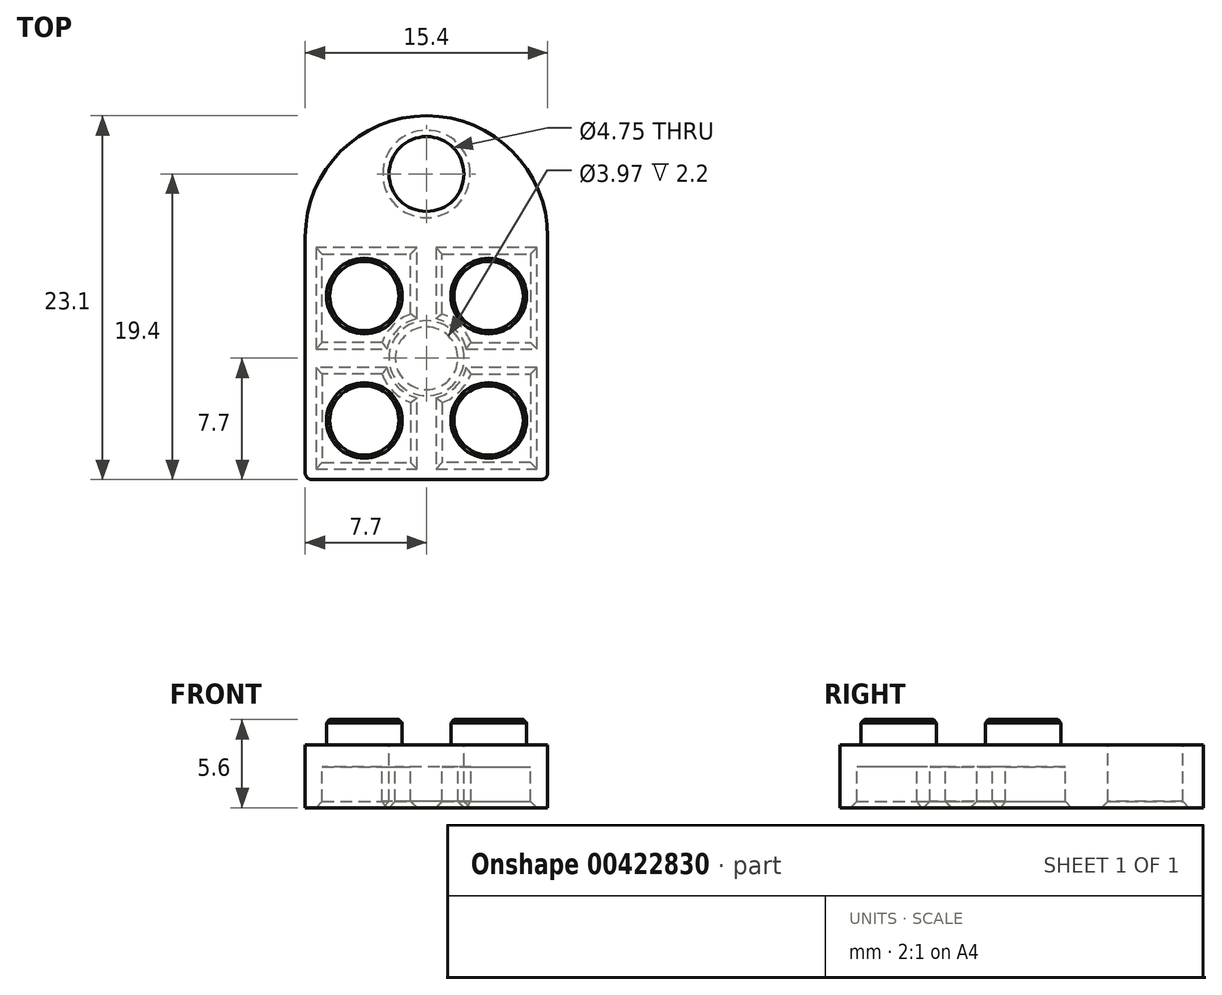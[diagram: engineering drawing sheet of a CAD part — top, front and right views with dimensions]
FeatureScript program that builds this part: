
annotation { "Feature Type Name" : "Feature", "Feature Type Description" : "" }
export const myFeature = defineFeature(function(context is Context, id is Id, definition is map)
    precondition{}
    {
        {
            var Q0;
            Q0=qCreatedBy(makeId("Top.planeOp"),FACE);
            var sketch = newSketch(context, id + "F0", { "sketchPlane" : qUnion([Q0])});
            skLineSegment(sketch, "E0.bottom", {"start": v(-7.7, 7.7) * mm, "end": v(7.7, 7.7) * mm});
            skLineSegment(sketch, "E0.top", {"start": v(-7.7, -7.7) * mm, "end": v(7.7, -7.7) * mm});
            skLineSegment(sketch, "E0.left", {"start": v(-7.7, 7.7) * mm, "end": v(-7.7, -7.7) * mm});
            skLineSegment(sketch, "E0.right", {"start": v(7.7, 7.7) * mm, "end": v(7.7, -7.7) * mm});
            skLineSegment(sketch, "E1", {"start": v(-7.7, 7.7) * mm, "end": v(7.7, -7.7) * mm, "construction": true});
            skArc(sketch, "E2", {"start": v(7.7, 7.7) * mm, "mid": v(0, 15.4) * mm, "end": v(-7.7, 7.7) * mm});
            skLineSegment(sketch, "E3", {"start": v(7.7, 7.7) * mm, "end": v(-7.7, -7.7) * mm, "construction": true});
            skLineSegment(sketch, "E4.bottom", {"start": v(-3.95, 3.95) * mm, "end": v(3.95, 3.95) * mm, "construction": true});
            skLineSegment(sketch, "E4.top", {"start": v(-3.95, -3.95) * mm, "end": v(3.95, -3.95) * mm, "construction": true});
            skLineSegment(sketch, "E4.left", {"start": v(-3.95, 3.95) * mm, "end": v(-3.95, -3.95) * mm, "construction": true});
            skLineSegment(sketch, "E4.right", {"start": v(3.95, 3.95) * mm, "end": v(3.95, -3.95) * mm, "construction": true});
            skCircle(sketch, "E5", {"center": v(3.95, 3.95) * mm, "radius": 2.4 * mm});
            skCircle(sketch, "E6", {"center": v(-3.95, 3.95) * mm, "radius": 2.4 * mm});
            skCircle(sketch, "E7", {"center": v(-3.95, -3.95) * mm, "radius": 2.4 * mm});
            skCircle(sketch, "E8", {"center": v(3.95, -3.95) * mm, "radius": 2.4 * mm});
            skLineSegment(sketch, "E9.bottom", {"start": v(-6.35, 6.35) * mm, "end": v(6.35, 6.35) * mm});
            skLineSegment(sketch, "E9.top", {"start": v(-6.35, -6.35) * mm, "end": v(6.35, -6.35) * mm});
            skLineSegment(sketch, "E9.left", {"start": v(-6.35, 6.35) * mm, "end": v(-6.35, -6.35) * mm});
            skLineSegment(sketch, "E9.right", {"start": v(6.35, 6.35) * mm, "end": v(6.35, -6.35) * mm});
            skCircle(sketch, "E10", {"center": v(0, 11.7) * mm, "radius": 2.38 * mm});
            skCircle(sketch, "E11", {"center": v(0, 0) * mm, "radius": 2.99 * mm});
            skCircle(sketch, "E12", {"center": v(0, 0) * mm, "radius": 1.99 * mm});
            skLineSegment(sketch, "E13.bottom", {"start": v(-6.62, 6.62) * mm, "end": v(6.62, 6.62) * mm});
            skLineSegment(sketch, "E13.top", {"start": v(-6.62, -6.62) * mm, "end": v(6.62, -6.62) * mm});
            skLineSegment(sketch, "E13.left", {"start": v(-6.62, 6.62) * mm, "end": v(-6.62, -6.62) * mm});
            skLineSegment(sketch, "E13.right", {"start": v(6.62, 6.62) * mm, "end": v(6.62, -6.62) * mm});
            skSolve(sketch);
        }
        {
            var Q0;
            Q0=makeQuery(id+"F0.imprint","IMPRINT",FACE,{"disambiguationData":[TD([[makeQuery(id+"F0.imprint","IMPRINT",EDGE,{"derivedFrom":sQuery(id+"F0.wireOp",EDGE,"E0.bottom")}),1.0]])]});
            var Q1;
            Q1=makeQuery(id+"F0.imprint","IMPRINT",FACE,{"disambiguationData":[TD([[makeQuery(id+"F0.imprint","IMPRINT",EDGE,{"derivedFrom":sQuery(id+"F0.wireOp",EDGE,"E5")}),1.0]])]});
            var Q2;
            Q2=makeQuery(id+"F0.imprint","IMPRINT",FACE,{"disambiguationData":[TD([[makeQuery(id+"F0.imprint","IMPRINT",EDGE,{"derivedFrom":sQuery(id+"F0.wireOp",EDGE,"E6")}),1.0]])]});
            var Q3;
            Q3=makeQuery(id+"F0.imprint","IMPRINT",FACE,{"disambiguationData":[TD([[makeQuery(id+"F0.imprint","IMPRINT",EDGE,{"derivedFrom":sQuery(id+"F0.wireOp",EDGE,"E7")}),1.0]])]});
            var Q4;
            Q4=makeQuery(id+"F0.imprint","IMPRINT",FACE,{"disambiguationData":[TD([[makeQuery(id+"F0.imprint","IMPRINT",EDGE,{"derivedFrom":sQuery(id+"F0.wireOp",EDGE,"E8")}),1.0]])]});
            var Q5;
            Q5=makeQuery(id+"F0.imprint","IMPRINT",FACE,{"disambiguationData":[TD([[makeQuery(id+"F0.imprint","IMPRINT",EDGE,{"derivedFrom":sQuery(id+"F0.wireOp",EDGE,"E0.bottom")}),-1.0]])]});
            var Q6;
            {var subQ5=sQuery(id+"F0.wireOp",EDGE,"E9.bottom");var subQ13=sQuery(id+"F0.wireOp",EDGE,"E5");var subQ14=makeQuery(id+"F0.imprint","INTERSECT",VERTEX,{"derivedFrom":[subQ13,subQ5]});Q6=makeQuery(id+"F0.imprint","IMPRINT",FACE,{"disambiguationData":[TD([[makeQuery(id+"F0.imprint","IMPRINT",EDGE,{"disambiguationData":[TD([[subQ14,-1.0]])],"derivedFrom":subQ13}),-1.0]])]});}
            var Q7;
            {var subQ0=sQuery(id+"F0.wireOp",EDGE,"E9.top");var subQ1=sQuery(id+"F0.wireOp",EDGE,"E7");var subQ2=makeQuery(id+"F0.imprint","INTERSECT",VERTEX,{"derivedFrom":[subQ1,subQ0]});Q7=makeQuery(id+"F0.imprint","IMPRINT",FACE,{"disambiguationData":[TD([[makeQuery(id+"F0.imprint","IMPRINT",EDGE,{"disambiguationData":[TD([[subQ2,1.0]])],"derivedFrom":subQ1}),-1.0]])]});}
            var Q8;
            {var subQ0=sQuery(id+"F0.wireOp",EDGE,"E9.bottom");var subQ1=sQuery(id+"F0.wireOp",EDGE,"E6");var subQ2=makeQuery(id+"F0.imprint","INTERSECT",VERTEX,{"derivedFrom":[subQ1,subQ0]});Q8=makeQuery(id+"F0.imprint","IMPRINT",FACE,{"disambiguationData":[TD([[makeQuery(id+"F0.imprint","IMPRINT",EDGE,{"disambiguationData":[TD([[subQ2,-1.0]])],"derivedFrom":subQ1}),-1.0]])]});}
            var Q9;
            {var subQ0=sQuery(id+"F0.wireOp",EDGE,"E9.bottom");var subQ1=sQuery(id+"F0.wireOp",EDGE,"E5");var subQ2=makeQuery(id+"F0.imprint","INTERSECT",VERTEX,{"derivedFrom":[subQ1,subQ0]});Q9=makeQuery(id+"F0.imprint","IMPRINT",FACE,{"disambiguationData":[TD([[makeQuery(id+"F0.imprint","IMPRINT",EDGE,{"disambiguationData":[TD([[subQ2,1.0]])],"derivedFrom":subQ1}),-1.0]])]});}
            var Q10;
            {var subQ0=sQuery(id+"F0.wireOp",EDGE,"E9.top");var subQ1=sQuery(id+"F0.wireOp",EDGE,"E8");var subQ2=makeQuery(id+"F0.imprint","INTERSECT",VERTEX,{"derivedFrom":[subQ1,subQ0]});Q10=makeQuery(id+"F0.imprint","IMPRINT",FACE,{"disambiguationData":[TD([[makeQuery(id+"F0.imprint","IMPRINT",EDGE,{"disambiguationData":[TD([[subQ2,-1.0]])],"derivedFrom":subQ1}),-1.0]])]});}
            var Q11;
            {var subQ0=sQuery(id+"F0.wireOp",EDGE,"E9.left");var subQ1=sQuery(id+"F0.wireOp",EDGE,"E6");var subQ2=makeQuery(id+"F0.imprint","INTERSECT",VERTEX,{"derivedFrom":[subQ1,subQ0]});Q11=makeQuery(id+"F0.imprint","IMPRINT",FACE,{"disambiguationData":[TD([[makeQuery(id+"F0.imprint","IMPRINT",EDGE,{"disambiguationData":[TD([[subQ2,-1.0]])],"derivedFrom":subQ1}),-1.0]])]});}
            var Q12;
            {var subQ0=sQuery(id+"F0.wireOp",EDGE,"E9.right");var subQ1=sQuery(id+"F0.wireOp",EDGE,"E5");var subQ2=makeQuery(id+"F0.imprint","INTERSECT",VERTEX,{"derivedFrom":[subQ1,subQ0]});Q12=makeQuery(id+"F0.imprint","IMPRINT",FACE,{"disambiguationData":[TD([[makeQuery(id+"F0.imprint","IMPRINT",EDGE,{"disambiguationData":[TD([[subQ2,1.0]])],"derivedFrom":subQ1}),-1.0]])]});}
            var Q13;
            {var subQ0=sQuery(id+"F0.wireOp",EDGE,"E11");var subQ1=sQuery(id+"F0.wireOp",EDGE,"E7");var subQ2=makeQuery(id+"F0.imprint","INTERSECT",VERTEX,{"derivedFrom":[subQ1,subQ0]});Q13=makeQuery(id+"F0.imprint","IMPRINT",FACE,{"disambiguationData":[TD([[makeQuery(id+"F0.imprint","IMPRINT",EDGE,{"disambiguationData":[TD([[subQ2,1.0]])],"derivedFrom":subQ1}),-1.0]])]});}
            var Q14;
            Q14=makeQuery(id+"F0.imprint","IMPRINT",FACE,{"disambiguationData":[TD([[makeQuery(id+"F0.imprint","IMPRINT",EDGE,{"derivedFrom":sQuery(id+"F0.wireOp",EDGE,"E12")}),-1.0]])]});
            var Q15;
            Q15=makeQuery(id+"F0.imprint","IMPRINT",FACE,{"disambiguationData":[TD([[makeQuery(id+"F0.imprint","IMPRINT",EDGE,{"derivedFrom":sQuery(id+"F0.wireOp",EDGE,"E12")}),1.0]])]});
            var Q16;
            Q16=makeQuery(id+"F0.imprint","IMPRINT",FACE,{"disambiguationData":[TD([[makeQuery(id+"F0.imprint","IMPRINT",EDGE,{"derivedFrom":sQuery(id+"F0.wireOp",EDGE,"E13.bottom")}),-1.0]])]});
            extrude(context, id + "F1", {"entities" : qUnion([Q0, Q1, Q2, Q3, Q4, Q5, Q6, Q7, Q8, Q9, Q10, Q11, Q12, Q13, Q14, Q15, Q16]), "oppositeDirection" : true, "depth" : 1.4 * mm});
        }
        {
            var Q0;
            Q0=makeQuery(id+"F0.imprint","IMPRINT",FACE,{"disambiguationData":[TD([[makeQuery(id+"F0.imprint","IMPRINT",EDGE,{"derivedFrom":sQuery(id+"F0.wireOp",EDGE,"E6")}),1.0]])]});
            var Q1;
            Q1=makeQuery(id+"F0.imprint","IMPRINT",FACE,{"disambiguationData":[TD([[makeQuery(id+"F0.imprint","IMPRINT",EDGE,{"derivedFrom":sQuery(id+"F0.wireOp",EDGE,"E5")}),1.0]])]});
            var Q2;
            Q2=makeQuery(id+"F0.imprint","IMPRINT",FACE,{"disambiguationData":[TD([[makeQuery(id+"F0.imprint","IMPRINT",EDGE,{"derivedFrom":sQuery(id+"F0.wireOp",EDGE,"E8")}),1.0]])]});
            var Q3;
            Q3=makeQuery(id+"F0.imprint","IMPRINT",FACE,{"disambiguationData":[TD([[makeQuery(id+"F0.imprint","IMPRINT",EDGE,{"derivedFrom":sQuery(id+"F0.wireOp",EDGE,"E7")}),1.0]])]});
            extrude(context, id + "F2", {"entities" : qUnion([Q0, Q1, Q2, Q3]), "operationType" : NewBodyOperationType.ADD, "depth" : 1.6 * mm});
        }
        {
            var Q0;
            Q0=makeQuery(id+"F0.imprint","IMPRINT",FACE,{"disambiguationData":[TD([[makeQuery(id+"F0.imprint","IMPRINT",EDGE,{"derivedFrom":sQuery(id+"F0.wireOp",EDGE,"E12")}),-1.0]])]});
            var Q1;
            Q1=makeQuery(id+"F0.imprint","IMPRINT",FACE,{"disambiguationData":[TD([[makeQuery(id+"F0.imprint","IMPRINT",EDGE,{"derivedFrom":sQuery(id+"F0.wireOp",EDGE,"E0.bottom")}),-1.0]])]});
            var Q2;
            Q2=makeQuery(id+"F0.imprint","IMPRINT",FACE,{"disambiguationData":[TD([[makeQuery(id+"F0.imprint","IMPRINT",EDGE,{"derivedFrom":sQuery(id+"F0.wireOp",EDGE,"E0.bottom")}),1.0]])]});
            extrude(context, id + "F3", {"entities" : qUnion([Q0, Q1, Q2]), "operationType" : NewBodyOperationType.ADD, "oppositeDirection" : true, "depth" : 4 * mm});
        }
        {
            var Q0;
            {var subQ0=sQuery(id+"F0.wireOp",EDGE,"E0.right");var subQ1=sQuery(id+"F0.wireOp",EDGE,"E0.top");Q0=makeQuery(id+"F3.boolean.opBoolean","MERGE",EDGE,{"derivedFrom":[makeQuery(id+"F1.opExtrude","SWEPT_EDGE",EDGE,{"disambiguationData":[OSD([subQ1,subQ0])]}),makeQuery(id+"F3.opExtrude","SWEPT_EDGE",EDGE,{"disambiguationData":[OSD([subQ1,subQ0])]})]});}
            var Q1;
            {var subQ0=sQuery(id+"F0.wireOp",EDGE,"E0.left");var subQ1=sQuery(id+"F0.wireOp",EDGE,"E0.top");Q1=makeQuery(id+"F3.boolean.opBoolean","MERGE",EDGE,{"derivedFrom":[makeQuery(id+"F1.opExtrude","SWEPT_EDGE",EDGE,{"disambiguationData":[OSD([subQ1,subQ0])]}),makeQuery(id+"F3.opExtrude","SWEPT_EDGE",EDGE,{"disambiguationData":[OSD([subQ1,subQ0])]})]});}
            fillet(context, id + "F4", {"entities" : qUnion([Q0, Q1]), "radius" : 0.4 * mm, "tangentPropagation" : true, "allowEdgeOverflow" : false});
        }
        {
            var Q0;
            Q0=makeQuery(id+"F3.boolean.opBoolean","SPLIT",FACE,{"disambiguationData":[TD([makeQuery(id+"F3.opExtrude","SWEPT_FACE",FACE,{"disambiguationData":[OSD([sQuery(id+"F0.wireOp",EDGE,"E11")])]})])],"derivedFrom":makeQuery(id+"F1.opExtrude","CAP_FACE",FACE,{"disambiguationData":[OSD([sQuery(id+"F0.wireOp",EDGE,"E0.top"),sQuery(id+"F0.wireOp",EDGE,"E0.left"),sQuery(id+"F0.wireOp",EDGE,"E0.right"),sQuery(id+"F0.wireOp",EDGE,"E2"),sQuery(id+"F0.wireOp",EDGE,"E10")])],"isStart":false})});
            var sketch = newSketch(context, id + "F5", { "sketchPlane" : qUnion([Q0])});
            skLineSegment(sketch, "E14.bottom", {"start": v(-1, 2.81) * mm, "end": v(1, 2.81) * mm});
            skLineSegment(sketch, "E14.top", {"start": v(-1, 6.62) * mm, "end": v(1, 6.62) * mm});
            skLineSegment(sketch, "E14.left", {"start": v(-1, 2.81) * mm, "end": v(-1, 6.62) * mm});
            skLineSegment(sketch, "E14.right", {"start": v(1, 2.81) * mm, "end": v(1, 6.62) * mm});
            skLineSegment(sketch, "E15.bottom", {"start": v(2.81, 1) * mm, "end": v(6.62, 1) * mm});
            skLineSegment(sketch, "E15.top", {"start": v(2.81, -1) * mm, "end": v(6.62, -1) * mm});
            skLineSegment(sketch, "E15.left", {"start": v(2.81, 1) * mm, "end": v(2.81, -1) * mm});
            skLineSegment(sketch, "E15.right", {"start": v(6.62, 1) * mm, "end": v(6.62, -1) * mm});
            skLineSegment(sketch, "E16.bottom", {"start": v(1, -2.81) * mm, "end": v(-1, -2.81) * mm});
            skLineSegment(sketch, "E16.top", {"start": v(1, -6.62) * mm, "end": v(-1, -6.62) * mm});
            skLineSegment(sketch, "E16.left", {"start": v(1, -2.81) * mm, "end": v(1, -6.62) * mm});
            skLineSegment(sketch, "E16.right", {"start": v(-1, -2.81) * mm, "end": v(-1, -6.62) * mm});
            skLineSegment(sketch, "E17.bottom", {"start": v(-2.81, -1) * mm, "end": v(-6.62, -1) * mm});
            skLineSegment(sketch, "E17.top", {"start": v(-2.81, 1) * mm, "end": v(-6.62, 1) * mm});
            skLineSegment(sketch, "E17.left", {"start": v(-2.81, -1) * mm, "end": v(-2.81, 1) * mm});
            skLineSegment(sketch, "E17.right", {"start": v(-6.62, -1) * mm, "end": v(-6.62, 1) * mm});
            skSolve(sketch);
        }
        {
            var Q0;
            {var subQ0=sQuery(id+"F5.wireOp",EDGE,"E17.bottom");Q0=makeQuery(id+"F5.imprint","IMPRINT",FACE,{"disambiguationData":[TD([[makeQuery(id+"F5.imprint","IMPRINT",EDGE,{"derivedFrom":subQ0}),-1.0]])]});}
            var Q1;
            Q1=makeQuery(id+"F5.imprint","IMPRINT",FACE,{"disambiguationData":[TD([[makeQuery(id+"F5.imprint","IMPRINT",EDGE,{"derivedFrom":sQuery(id+"F5.wireOp",EDGE,"E14.top")}),-1.0]])]});
            var Q2;
            {var subQ0=sQuery(id+"F5.wireOp",EDGE,"E15.bottom");Q2=makeQuery(id+"F5.imprint","IMPRINT",FACE,{"disambiguationData":[TD([[makeQuery(id+"F5.imprint","IMPRINT",EDGE,{"derivedFrom":subQ0}),-1.0]])]});}
            var Q3;
            Q3=makeQuery(id+"F5.imprint","IMPRINT",FACE,{"disambiguationData":[TD([[makeQuery(id+"F5.imprint","IMPRINT",EDGE,{"derivedFrom":sQuery(id+"F5.wireOp",EDGE,"E16.top")}),1.0]])]});
            var Q4;
            Q4=makeQuery(id+"F3.opExtrude","CAP_FACE",FACE,{"disambiguationData":[OSD([sQuery(id+"F0.wireOp",EDGE,"E11"),sQuery(id+"F0.wireOp",EDGE,"E12")])],"isStart":false});
            extrude(context, id + "F6", {"entities" : qUnion([Q0, Q1, Q2, Q3]), "operationType" : NewBodyOperationType.ADD, "endBound" : BoundingType.UP_TO_SURFACE, "endBoundEntityFace" : qUnion([Q4]), "depth" : 25 * mm});
        }
        {
            var Q0;
            Q0=makeQuery(id+"F2.opExtrude","CAP_FACE",FACE,{"disambiguationData":[OSD([sQuery(id+"F0.wireOp",EDGE,"E7")])],"isStart":false});
            var Q1;
            Q1=makeQuery(id+"F2.opExtrude","CAP_FACE",FACE,{"disambiguationData":[OSD([sQuery(id+"F0.wireOp",EDGE,"E6")])],"isStart":false});
            var Q2;
            Q2=makeQuery(id+"F2.opExtrude","CAP_EDGE",EDGE,{"disambiguationData":[OSD([sQuery(id+"F0.wireOp",EDGE,"E5")])],"isStart":false});
            var Q3;
            Q3=makeQuery(id+"F2.opExtrude","CAP_FACE",FACE,{"disambiguationData":[OSD([sQuery(id+"F0.wireOp",EDGE,"E8")])],"isStart":false});
            chamfer(context, id + "F7", {"entities" : qUnion([Q0, Q1, Q2, Q3]), "width" : 0.2 * mm, "tangentPropagation" : true});
        }
        {
            var Q0;
            {var subQ0=sQuery(id+"F0.wireOp",EDGE,"E13.left");var subQ1=sQuery(id+"F0.wireOp",EDGE,"E13.top");Q0=makeQuery(id+"F6.boolean.opBoolean","SPLIT",EDGE,{"disambiguationData":[TD([makeQuery(id+"F3.opExtrude","SWEPT_FACE",FACE,{"disambiguationData":[OSD([subQ1])]})])],"derivedFrom":makeQuery(id+"F3.opExtrude","CAP_EDGE",EDGE,{"disambiguationData":[OSD([subQ0])],"isStart":false})});}
            var Q1;
            {var subQ0=sQuery(id+"F0.wireOp",EDGE,"E13.left");var subQ1=sQuery(id+"F0.wireOp",EDGE,"E13.top");Q1=makeQuery(id+"F6.boolean.opBoolean","SPLIT",EDGE,{"disambiguationData":[TD([makeQuery(id+"F3.opExtrude","SWEPT_FACE",FACE,{"disambiguationData":[OSD([subQ0])]})])],"derivedFrom":makeQuery(id+"F3.opExtrude","CAP_EDGE",EDGE,{"disambiguationData":[OSD([subQ1])],"isStart":false})});}
            var Q2;
            Q2=makeQuery(id+"F6.opExtrude","CAP_EDGE",EDGE,{"disambiguationData":[OSD([sQuery(id+"F5.wireOp",EDGE,"E14.left")])],"isStart":false});
            var Q3;
            {var subQ0=sQuery(id+"F0.wireOp",EDGE,"E11");var subQ1=sQuery(id+"F5.wireOp",EDGE,"E14.left");Q3=makeQuery(id+"F6.boolean.opBoolean","SPLIT",EDGE,{"disambiguationData":[TD([makeQuery(id+"F6.opExtrude","SWEPT_FACE",FACE,{"disambiguationData":[OSD([subQ1])]})])],"derivedFrom":makeQuery(id+"F3.opExtrude","CAP_EDGE",EDGE,{"disambiguationData":[OSD([subQ0])],"isStart":false})});}
            var Q4;
            Q4=makeQuery(id+"F6.opExtrude","CAP_EDGE",EDGE,{"disambiguationData":[OSD([sQuery(id+"F5.wireOp",EDGE,"E17.top")])],"isStart":false});
            var Q5;
            {var subQ0=sQuery(id+"F0.wireOp",EDGE,"E11");var subQ1=sQuery(id+"F5.wireOp",EDGE,"E14.right");Q5=makeQuery(id+"F6.boolean.opBoolean","SPLIT",EDGE,{"disambiguationData":[TD([makeQuery(id+"F6.opExtrude","SWEPT_FACE",FACE,{"disambiguationData":[OSD([subQ1])]})])],"derivedFrom":makeQuery(id+"F3.opExtrude","CAP_EDGE",EDGE,{"disambiguationData":[OSD([subQ0])],"isStart":false})});}
            var Q6;
            Q6=makeQuery(id+"F6.opExtrude","CAP_EDGE",EDGE,{"disambiguationData":[OSD([sQuery(id+"F5.wireOp",EDGE,"E15.bottom")])],"isStart":false});
            var Q7;
            {var subQ0=sQuery(id+"F0.wireOp",EDGE,"E13.right");var subQ3=sQuery(id+"F0.wireOp",EDGE,"E13.top");Q7=makeQuery(id+"F6.boolean.opBoolean","SPLIT",EDGE,{"disambiguationData":[TD([makeQuery(id+"F3.opExtrude","SWEPT_FACE",FACE,{"disambiguationData":[OSD([subQ3])]})])],"derivedFrom":makeQuery(id+"F3.opExtrude","CAP_EDGE",EDGE,{"disambiguationData":[OSD([subQ0])],"isStart":false})});}
            var Q8;
            {var subQ0=sQuery(id+"F0.wireOp",EDGE,"E13.right");var subQ2=sQuery(id+"F0.wireOp",EDGE,"E13.top");Q8=makeQuery(id+"F6.boolean.opBoolean","SPLIT",EDGE,{"disambiguationData":[TD([makeQuery(id+"F3.opExtrude","SWEPT_FACE",FACE,{"disambiguationData":[OSD([subQ0])]})])],"derivedFrom":makeQuery(id+"F3.opExtrude","CAP_EDGE",EDGE,{"disambiguationData":[OSD([subQ2])],"isStart":false})});}
            var Q9;
            Q9=makeQuery(id+"F6.opExtrude","CAP_EDGE",EDGE,{"disambiguationData":[OSD([sQuery(id+"F5.wireOp",EDGE,"E14.right")])],"isStart":false});
            var Q10;
            Q10=makeQuery(id+"F6.opExtrude","CAP_EDGE",EDGE,{"disambiguationData":[OSD([sQuery(id+"F5.wireOp",EDGE,"E15.top")])],"isStart":false});
            var Q11;
            {var subQ0=sQuery(id+"F0.wireOp",EDGE,"E11");var subQ7=sQuery(id+"F5.wireOp",EDGE,"E15.top");Q11=makeQuery(id+"F6.boolean.opBoolean","SPLIT",EDGE,{"disambiguationData":[TD([makeQuery(id+"F6.opExtrude","SWEPT_FACE",FACE,{"disambiguationData":[OSD([subQ7])]})])],"derivedFrom":makeQuery(id+"F3.opExtrude","CAP_EDGE",EDGE,{"disambiguationData":[OSD([subQ0])],"isStart":false})});}
            var Q12;
            Q12=makeQuery(id+"F6.opExtrude","CAP_EDGE",EDGE,{"disambiguationData":[OSD([sQuery(id+"F5.wireOp",EDGE,"E16.left")])],"isStart":false});
            var Q13;
            {var subQ0=sQuery(id+"F0.wireOp",EDGE,"E13.bottom");var subQ8=sQuery(id+"F0.wireOp",EDGE,"E13.right");Q13=makeQuery(id+"F6.boolean.opBoolean","SPLIT",EDGE,{"disambiguationData":[TD([makeQuery(id+"F3.opExtrude","SWEPT_FACE",FACE,{"disambiguationData":[OSD([subQ8])]})])],"derivedFrom":makeQuery(id+"F3.opExtrude","CAP_EDGE",EDGE,{"disambiguationData":[OSD([subQ0])],"isStart":false})});}
            var Q14;
            {var subQ0=sQuery(id+"F0.wireOp",EDGE,"E13.bottom");var subQ7=sQuery(id+"F0.wireOp",EDGE,"E13.right");Q14=makeQuery(id+"F6.boolean.opBoolean","SPLIT",EDGE,{"disambiguationData":[TD([makeQuery(id+"F3.opExtrude","SWEPT_FACE",FACE,{"disambiguationData":[OSD([subQ0])]})])],"derivedFrom":makeQuery(id+"F3.opExtrude","CAP_EDGE",EDGE,{"disambiguationData":[OSD([subQ7])],"isStart":false})});}
            var Q15;
            Q15=makeQuery(id+"F6.opExtrude","CAP_EDGE",EDGE,{"disambiguationData":[OSD([sQuery(id+"F5.wireOp",EDGE,"E16.right")])],"isStart":false});
            var Q16;
            {var subQ0=sQuery(id+"F0.wireOp",EDGE,"E11");var subQ7=sQuery(id+"F5.wireOp",EDGE,"E16.right");Q16=makeQuery(id+"F6.boolean.opBoolean","SPLIT",EDGE,{"disambiguationData":[TD([makeQuery(id+"F6.opExtrude","SWEPT_FACE",FACE,{"disambiguationData":[OSD([subQ7])]})])],"derivedFrom":makeQuery(id+"F3.opExtrude","CAP_EDGE",EDGE,{"disambiguationData":[OSD([subQ0])],"isStart":false})});}
            var Q17;
            Q17=makeQuery(id+"F6.opExtrude","CAP_EDGE",EDGE,{"disambiguationData":[OSD([sQuery(id+"F5.wireOp",EDGE,"E17.bottom")])],"isStart":false});
            var Q18;
            {var subQ0=sQuery(id+"F0.wireOp",EDGE,"E13.left");var subQ1=sQuery(id+"F0.wireOp",EDGE,"E13.bottom");Q18=makeQuery(id+"F6.boolean.opBoolean","SPLIT",EDGE,{"disambiguationData":[TD([makeQuery(id+"F3.opExtrude","SWEPT_FACE",FACE,{"disambiguationData":[OSD([subQ1])]})])],"derivedFrom":makeQuery(id+"F3.opExtrude","CAP_EDGE",EDGE,{"disambiguationData":[OSD([subQ0])],"isStart":false})});}
            var Q19;
            {var subQ0=sQuery(id+"F0.wireOp",EDGE,"E13.left");var subQ1=sQuery(id+"F0.wireOp",EDGE,"E13.bottom");Q19=makeQuery(id+"F6.boolean.opBoolean","SPLIT",EDGE,{"disambiguationData":[TD([makeQuery(id+"F3.opExtrude","SWEPT_FACE",FACE,{"disambiguationData":[OSD([subQ0])]})])],"derivedFrom":makeQuery(id+"F3.opExtrude","CAP_EDGE",EDGE,{"disambiguationData":[OSD([subQ1])],"isStart":false})});}
            var Q20;
            Q20=makeQuery(id+"F3.opExtrude","CAP_EDGE",EDGE,{"disambiguationData":[OSD([sQuery(id+"F0.wireOp",EDGE,"E10")])],"isStart":false});
            var Q21;
            Q21=makeQuery(id+"F3.opExtrude","CAP_EDGE",EDGE,{"disambiguationData":[OSD([sQuery(id+"F0.wireOp",EDGE,"E12")])],"isStart":false});
            chamfer(context, id + "F8", {"entities" : qUnion([Q0, Q1, Q2, Q3, Q4, Q5, Q6, Q7, Q8, Q9, Q10, Q11, Q12, Q13, Q14, Q15, Q16, Q17, Q18, Q19, Q20, Q21]), "width" : 0.4 * mm, "tangentPropagation" : true});
        }
    });
